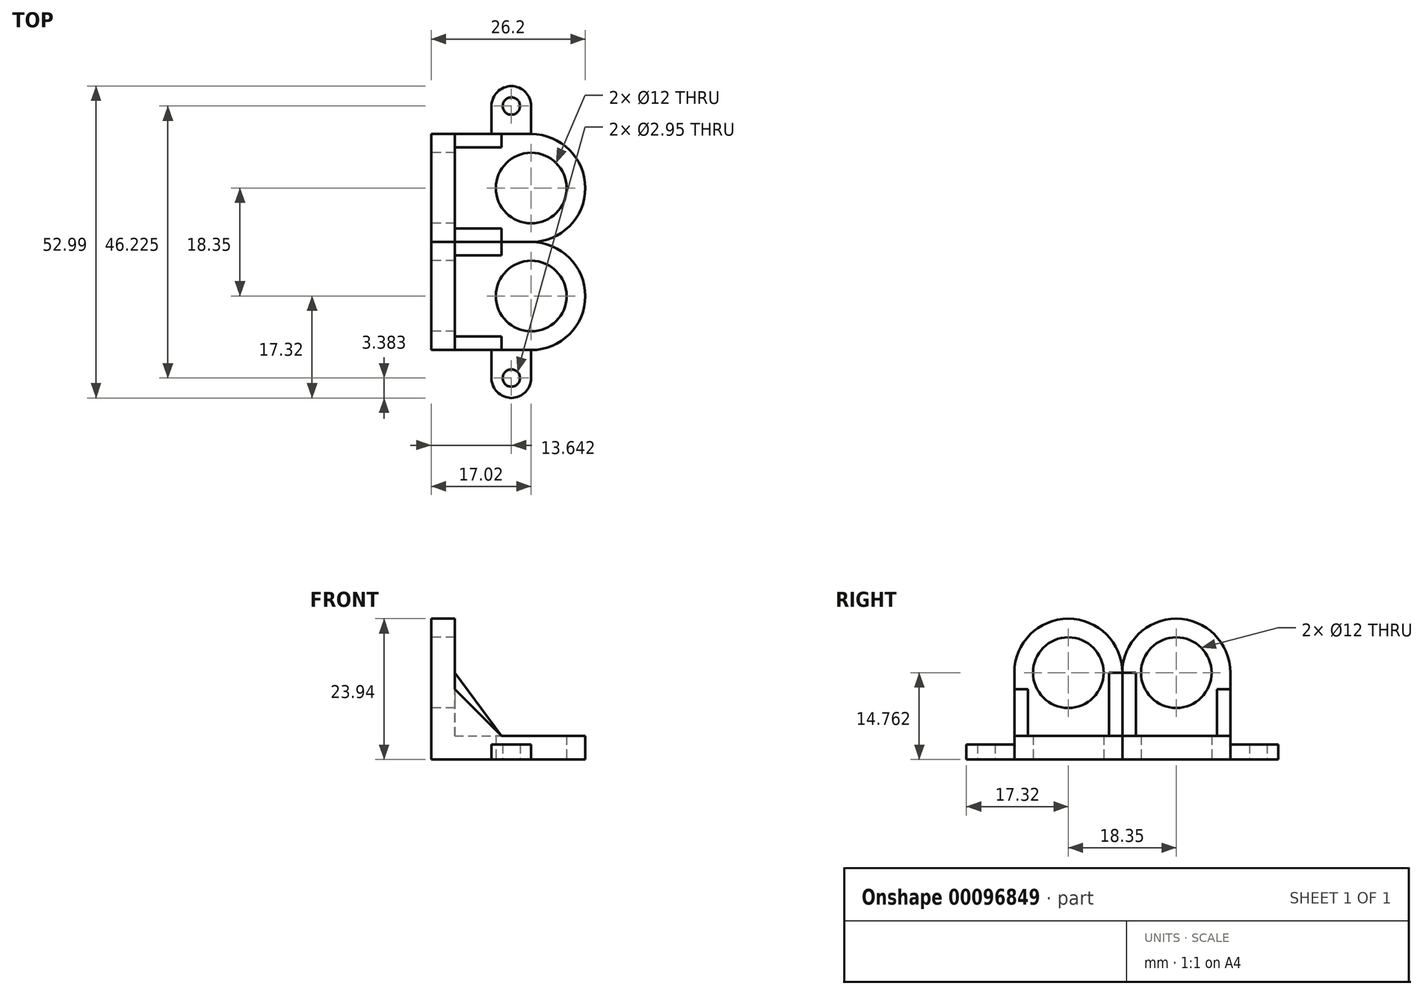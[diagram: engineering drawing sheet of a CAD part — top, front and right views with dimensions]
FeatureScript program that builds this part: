
annotation { "Feature Type Name" : "Feature", "Feature Type Description" : "" }
export const myFeature = defineFeature(function(context is Context, id is Id, definition is map)
    precondition{}
    {
        {
            var Q0;
            Q0=qCreatedBy(makeId("Top.planeOp"),FACE);
            var sketch = newSketch(context, id + "F0", { "sketchPlane" : qUnion([Q0])});
            skCircle(sketch, "E0", {"center": v(0, 0) * mm, "radius": 6 * mm});
            skArc(sketch, "E1", {"start": v(0, 9.18) * mm, "mid": v(9.18, 0) * mm, "end": v(0, -9.18) * mm});
            skLineSegment(sketch, "E2", {"start": v(0, 9.18) * mm, "end": v(-17.02, 9.18) * mm});
            skLineSegment(sketch, "E3", {"start": v(-17.02, 9.17) * mm, "end": v(-17.02, -9.18) * mm});
            skLineSegment(sketch, "E4", {"start": v(-17.02, -9.18) * mm, "end": v(0, -9.18) * mm});
            skSolve(sketch);
        }
        {
            var Q0;
            Q0 = qSketchRegion(id + "F0", true);
            extrude(context, id + "F1", {"entities" : qUnion([Q0]), "depth" : 4 * mm});
        }
        {
            var Q0;
            Q0=makeQuery(id+"F1.opExtrude","SWEPT_FACE",FACE,{"disambiguationData":[OSD([sQuery(id+"F0.wireOp",EDGE,"E3")])]});
            var sketch = newSketch(context, id + "F2", { "sketchPlane" : qUnion([Q0])});
            skCircle(sketch, "E5", {"center": v(0, 14.76) * mm, "radius": 6 * mm});
            skArc(sketch, "E6", {"start": v(-9.17, 14.76) * mm, "mid": v(0, 23.94) * mm, "end": v(9.17, 14.76) * mm});
            skLineSegment(sketch, "E7", {"start": v(-9.17, 14.76) * mm, "end": v(-9.18, 4) * mm});
            skLineSegment(sketch, "E8", {"start": v(-9.18, 4) * mm, "end": v(9.18, 4) * mm});
            skLineSegment(sketch, "E9", {"start": v(9.17, 4) * mm, "end": v(9.17, 14.76) * mm});
            skSolve(sketch);
        }
        {
            var Q0;
            Q0 = qSketchRegion(id + "F2", true);
            extrude(context, id + "F3", {"entities" : qUnion([Q0]), "operationType" : NewBodyOperationType.ADD, "oppositeDirection" : true, "depth" : 4 * mm});
        }
        {
            var Q0;
            Q0=makeQuery(id+"F3.boolean.opBoolean","MERGE",FACE,{"derivedFrom":[makeQuery(id+"F1.opExtrude","SWEPT_FACE",FACE,{"disambiguationData":[OSD([sQuery(id+"F0.wireOp",EDGE,"E4")])]}),makeQuery(id+"F3.opExtrude","SWEPT_FACE",FACE,{"disambiguationData":[OSD([sQuery(id+"F2.wireOp",EDGE,"E9")])]})]});
            var sketch = newSketch(context, id + "F4", { "sketchPlane" : qUnion([Q0])});
            skLineSegment(sketch, "E10", {"start": v(-13.02, 11.94) * mm, "end": v(-5.08, 4) * mm});
            skLineSegment(sketch, "E11", {"start": v(-5.08, 4) * mm, "end": v(-13.02, 4) * mm});
            skLineSegment(sketch, "E12", {"start": v(-13.02, 4) * mm, "end": v(-13.02, 11.94) * mm});
            skSolve(sketch);
        }
        {
            var Q0;
            Q0 = qSketchRegion(id + "F4", true);
            extrude(context, id + "F5", {"entities" : qUnion([Q0]), "operationType" : NewBodyOperationType.ADD, "oppositeDirection" : true, "depth" : 2.3 * mm});
        }
        {
            var Q0;
            Q0=makeQuery(id+"F3.boolean.opBoolean","MERGE",FACE,{"derivedFrom":[makeQuery(id+"F1.opExtrude","SWEPT_FACE",FACE,{"disambiguationData":[OSD([sQuery(id+"F0.wireOp",EDGE,"E2")])]}),makeQuery(id+"F3.opExtrude","SWEPT_FACE",FACE,{"disambiguationData":[OSD([sQuery(id+"F2.wireOp",EDGE,"E7")])]})]});
            var sketch = newSketch(context, id + "F6", { "sketchPlane" : qUnion([Q0])});
            skLineSegment(sketch, "E13", {"start": v(13.02, 14.76) * mm, "end": v(5.08, 4) * mm});
            skLineSegment(sketch, "E14", {"start": v(5.08, 4) * mm, "end": v(13.02, 4) * mm});
            skLineSegment(sketch, "E15", {"start": v(13.02, 4) * mm, "end": v(13.02, 14.76) * mm});
            skSolve(sketch);
        }
        {
            var Q0;
            Q0 = qSketchRegion(id + "F6", true);
            extrude(context, id + "F7", {"entities" : qUnion([Q0]), "operationType" : NewBodyOperationType.ADD, "oppositeDirection" : true, "depth" : 2.3 * mm});
        }
        {
            var Q0;
            Q0=makeQuery(id+"F1.opExtrude","CAP_FACE",FACE,{"disambiguationData":[OSD([sQuery(id+"F0.wireOp",EDGE,"E0"),sQuery(id+"F0.wireOp",EDGE,"E1"),sQuery(id+"F0.wireOp",EDGE,"E2"),sQuery(id+"F0.wireOp",EDGE,"E3"),sQuery(id+"F0.wireOp",EDGE,"E4")])],"isStart":true});
            var sketch = newSketch(context, id + "F8", { "sketchPlane" : qUnion([Q0])});
            skCircle(sketch, "E16", {"center": v(-3.38, 13.94) * mm, "radius": 1.47 * mm});
            skArc(sketch, "E17", {"start": v(-6.76, 13.94) * mm, "mid": v(-3.38, 17.32) * mm, "end": v(0, 13.94) * mm});
            skLineSegment(sketch, "E18", {"start": v(-6.76, 13.94) * mm, "end": v(-6.76, 9.18) * mm});
            skLineSegment(sketch, "E19", {"start": v(-6.76, 9.18) * mm, "end": v(0, 9.18) * mm});
            skLineSegment(sketch, "E20", {"start": v(0, 9.18) * mm, "end": v(0, 13.94) * mm});
            skSolve(sketch);
        }
        {
            var Q0;
            Q0 = qSketchRegion(id + "F8", true);
            extrude(context, id + "F9", {"entities" : qUnion([Q0]), "operationType" : NewBodyOperationType.ADD, "oppositeDirection" : true, "depth" : 2.54 * mm});
        }
        {
            var Q0;
            Q0=makeQuery(id+"F1.opExtrude","SWEPT_BODY",BODY,{"disambiguationData":[OSD([sQuery(id+"F0.wireOp",EDGE,"E0"),sQuery(id+"F0.wireOp",EDGE,"E1"),sQuery(id+"F0.wireOp",EDGE,"E2"),sQuery(id+"F0.wireOp",EDGE,"E3"),sQuery(id+"F0.wireOp",EDGE,"E4")])]});
            var Q1;
            Q1=makeQuery(id+"F7.boolean.opBoolean","MERGE",FACE,{"derivedFrom":[makeQuery(id+"F3.boolean.opBoolean","MERGE",FACE,{"derivedFrom":[makeQuery(id+"F1.opExtrude","SWEPT_FACE",FACE,{"disambiguationData":[OSD([sQuery(id+"F0.wireOp",EDGE,"E2")])]}),makeQuery(id+"F3.opExtrude","SWEPT_FACE",FACE,{"disambiguationData":[OSD([sQuery(id+"F2.wireOp",EDGE,"E7")])]})]}),makeQuery(id+"F7.opExtrude","CAP_FACE",FACE,{"disambiguationData":[OSD([sQuery(id+"F6.wireOp",EDGE,"E13"),sQuery(id+"F6.wireOp",EDGE,"E14"),sQuery(id+"F6.wireOp",EDGE,"E15")])],"isStart":true})]});
            mirror(context, id + "F10", {"entities" : qUnion([Q0]), "mirrorPlane" : qUnion([Q1])});
        }
    });
